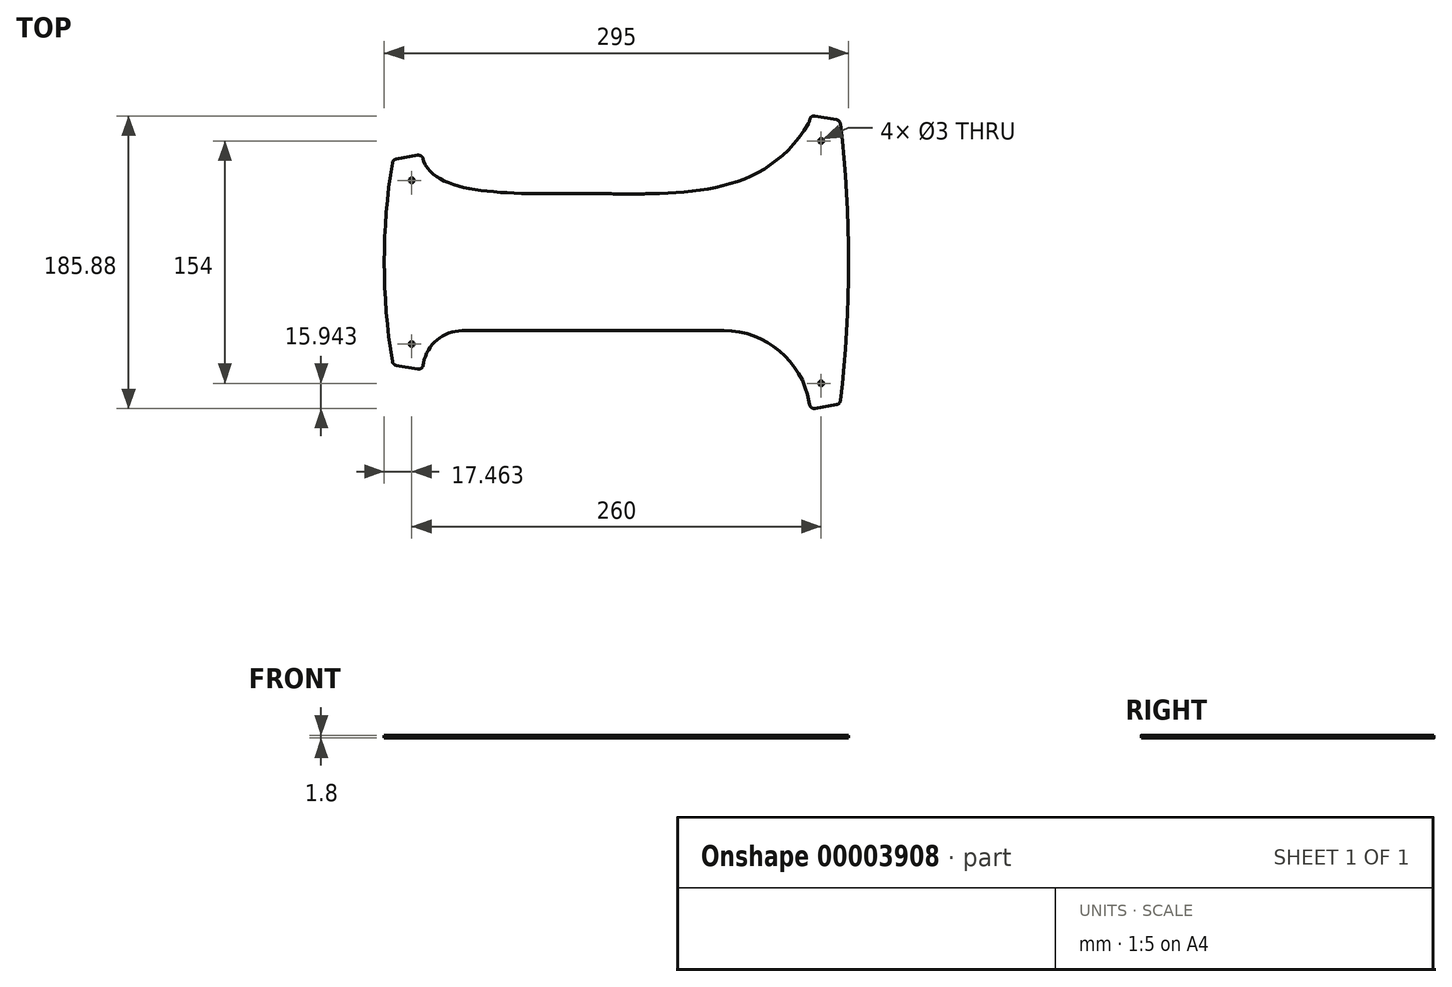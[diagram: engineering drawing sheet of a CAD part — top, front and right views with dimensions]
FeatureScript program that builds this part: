
annotation { "Feature Type Name" : "Feature", "Feature Type Description" : "" }
export const myFeature = defineFeature(function(context is Context, id is Id, definition is map)
    precondition{}
    {
        {
            var Q0;
            Q0=qCreatedBy(makeId("Top.planeOp"),FACE);
            var sketch = newSketch(context, id + "F0", { "sketchPlane" : qUnion([Q0])});
            skCircle(sketch, "E0", {"center": v(-144.57, -75.39) * mm, "radius": 1.5 * mm});
            skCircle(sketch, "E1", {"center": v(115.43, -100.39) * mm, "radius": 1.5 * mm});
            skLineSegment(sketch, "E2", {"start": v(132.97, -23.39) * mm, "end": v(-162.03, -23.39) * mm});
            skLineSegment(sketch, "E3", {"start": v(-154.44, -88.88) * mm, "end": v(-140.77, -91.29) * mm});
            skLineSegment(sketch, "E4", {"start": v(-137.3, -88.85) * mm, "end": v(-135.21, -77.04) * mm});
            skLineSegment(sketch, "E5", {"start": v(-135.21, -77.04) * mm, "end": v(-153.92, -73.74) * mm});
            skLineSegment(sketch, "E6", {"start": v(-153.92, -73.74) * mm, "end": v(-156.53, -88.5) * mm});
            skLineSegment(sketch, "E7", {"start": v(-137.06, -87.55) * mm, "end": v(-135.21, -77.04) * mm});
            skLineSegment(sketch, "E8", {"start": v(-112.44, -66.89) * mm, "end": v(53.73, -66.89) * mm});
            skLineSegment(sketch, "E9", {"start": v(-144.57, -75.39) * mm, "end": v(-171.48, -228.03) * mm});
            skLineSegment(sketch, "E10", {"start": v(106.08, -102.04) * mm, "end": v(124.79, -98.74) * mm});
            skLineSegment(sketch, "E11", {"start": v(124.79, -98.74) * mm, "end": v(127.4, -113.5) * mm});
            skLineSegment(sketch, "E12", {"start": v(125.2, -113.9) * mm, "end": v(111.64, -116.29) * mm});
            skLineSegment(sketch, "E13", {"start": v(108.16, -113.85) * mm, "end": v(106.08, -102.04) * mm});
            skLineSegment(sketch, "E14", {"start": v(115.43, -100.39) * mm, "end": v(138, -228.41) * mm});
            skLineSegment(sketch, "E15", {"start": v(107.9, -112.34) * mm, "end": v(106.08, -102.04) * mm});
            skPoint(sketch, "E16", {"position": v(122.82, -99.08) * mm});
            skPoint(sketch, "E17", {"position": v(108.05, -101.69) * mm});
            skLineSegment(sketch, "E18", {"start": v(108.05, -101.69) * mm, "end": v(99.36, -52.45) * mm});
            skLineSegment(sketch, "E19", {"start": v(99.36, -52.45) * mm, "end": v(114.14, -49.84) * mm});
            skLineSegment(sketch, "E20", {"start": v(114.14, -49.84) * mm, "end": v(122.82, -99.08) * mm});
            skPoint(sketch, "E21", {"position": v(-137.18, -76.69) * mm});
            skPoint(sketch, "E22", {"position": v(-151.95, -74.08) * mm});
            skLineSegment(sketch, "E23", {"start": v(-151.95, -74.08) * mm, "end": v(-144.14, -29.77) * mm});
            skLineSegment(sketch, "E24", {"start": v(-144.14, -29.77) * mm, "end": v(-129.37, -32.37) * mm});
            skLineSegment(sketch, "E25", {"start": v(-129.37, -32.37) * mm, "end": v(-137.18, -76.69) * mm});
            skCircle(sketch, "E26", {"center": v(-168, -208.34) * mm, "radius": 50 * mm});
            skCircle(sketch, "E27", {"center": v(134.53, -208.72) * mm, "radius": 50 * mm});
            skCircle(sketch, "E28", {"center": v(-144.57, 28.61) * mm, "radius": 1.5 * mm});
            skLineSegment(sketch, "E29", {"start": v(-144.14, -17) * mm, "end": v(-129.37, -14.4) * mm});
            skLineSegment(sketch, "E30", {"start": v(-129.37, -14.4) * mm, "end": v(-137.18, 29.92) * mm});
            skLineSegment(sketch, "E31", {"start": v(-137.18, 29.92) * mm, "end": v(-151.95, 27.31) * mm});
            skLineSegment(sketch, "E32", {"start": v(-151.95, 27.31) * mm, "end": v(-144.14, -17) * mm});
            skLineSegment(sketch, "E33", {"start": v(-137.18, 29.92) * mm, "end": v(-135.21, 30.26) * mm});
            skLineSegment(sketch, "E34", {"start": v(-151.95, 27.31) * mm, "end": v(-153.92, 26.96) * mm});
            skLineSegment(sketch, "E35", {"start": v(-135.21, 30.26) * mm, "end": v(-137.3, 42.08) * mm});
            skLineSegment(sketch, "E36", {"start": v(-140.77, 44.51) * mm, "end": v(-154.44, 42.1) * mm});
            skLineSegment(sketch, "E37", {"start": v(-156.53, 41.74) * mm, "end": v(-153.92, 26.96) * mm});
            skLineSegment(sketch, "E38", {"start": v(-112.44, 20.11) * mm, "end": v(53.73, 20.11) * mm});
            skLineSegment(sketch, "E39", {"start": v(-137.06, 40.77) * mm, "end": v(-135.21, 30.26) * mm});
            skCircle(sketch, "E40", {"center": v(115.43, 53.61) * mm, "radius": 1.5 * mm});
            skLineSegment(sketch, "E41", {"start": v(122.82, 52.31) * mm, "end": v(108.05, 54.92) * mm});
            skLineSegment(sketch, "E42", {"start": v(108.05, 54.92) * mm, "end": v(99.36, 5.68) * mm});
            skLineSegment(sketch, "E43", {"start": v(99.36, 5.68) * mm, "end": v(114.14, 3.07) * mm});
            skLineSegment(sketch, "E44", {"start": v(114.14, 3.07) * mm, "end": v(122.82, 52.31) * mm});
            skLineSegment(sketch, "E45", {"start": v(122.82, 52.31) * mm, "end": v(124.79, 51.96) * mm});
            skLineSegment(sketch, "E46", {"start": v(108.05, 54.92) * mm, "end": v(106.08, 55.26) * mm});
            skLineSegment(sketch, "E47", {"start": v(108.17, 66.78) * mm, "end": v(108.22, 67.07) * mm});
            skLineSegment(sketch, "E48", {"start": v(111.7, 69.5) * mm, "end": v(125.2, 67.12) * mm});
            skLineSegment(sketch, "E49", {"start": v(127.4, 66.74) * mm, "end": v(124.79, 51.96) * mm});
            skLineSegment(sketch, "E50", {"start": v(107.9, 65.56) * mm, "end": v(106.08, 55.26) * mm});
            skArc(sketch, "E51", {"start": v(-156.88, 39.64) * mm, "mid": v(-162.03, -23.39) * mm, "end": v(-156.88, -86.4) * mm});
            skArc(sketch, "E52", {"start": v(127.66, -111.3) * mm, "mid": v(132.97, -23.39) * mm, "end": v(127.66, 64.53) * mm});
            skPoint(sketch, "E53.visualSharp", {"position": v(-156.53, 41.74) * mm});
            skArc(sketch, "E53.filletArc", {"start": v(-154.44, 42.1) * mm, "mid": v(-156.05, 41.26) * mm, "end": v(-156.88, 39.64) * mm});
            skPoint(sketch, "E54.visualSharp", {"position": v(-137.82, 45.04) * mm});
            skArc(sketch, "E54.filletArc", {"start": v(-137.3, 42.08) * mm, "mid": v(-138.53, 44.02) * mm, "end": v(-140.77, 44.51) * mm});
            skPoint(sketch, "E55.visualSharp", {"position": v(-133.42, 20.11) * mm});
            skArc(sketch, "E55.filletArc", {"start": v(-137.06, 40.77) * mm, "mid": v(-128.51, 25.96) * mm, "end": v(-112.44, 20.11) * mm});
            skPoint(sketch, "E56.visualSharp", {"position": v(99.88, 20.11) * mm});
            skArc(sketch, "E56.filletArc", {"start": v(53.73, 20.11) * mm, "mid": v(89.08, 32.98) * mm, "end": v(107.9, 65.56) * mm});
            skPoint(sketch, "E57.visualSharp", {"position": v(108.75, 70.02) * mm});
            skArc(sketch, "E57.filletArc", {"start": v(111.7, 69.5) * mm, "mid": v(109.46, 69) * mm, "end": v(108.22, 67.07) * mm});
            skPoint(sketch, "E58.visualSharp", {"position": v(127.4, 66.74) * mm});
            skArc(sketch, "E58.filletArc", {"start": v(127.66, 64.53) * mm, "mid": v(126.86, 66.23) * mm, "end": v(125.2, 67.12) * mm});
            skPoint(sketch, "E59.visualSharp", {"position": v(127.4, -113.5) * mm});
            skArc(sketch, "E59.filletArc", {"start": v(125.2, -113.9) * mm, "mid": v(126.86, -113) * mm, "end": v(127.66, -111.3) * mm});
            skPoint(sketch, "E60.visualSharp", {"position": v(108.68, -116.8) * mm});
            skArc(sketch, "E60.filletArc", {"start": v(108.16, -113.85) * mm, "mid": v(109.4, -115.8) * mm, "end": v(111.64, -116.29) * mm});
            skPoint(sketch, "E61.visualSharp", {"position": v(99.88, -66.89) * mm});
            skArc(sketch, "E61.filletArc", {"start": v(107.9, -112.34) * mm, "mid": v(89.08, -79.75) * mm, "end": v(53.73, -66.89) * mm});
            skPoint(sketch, "E62.visualSharp", {"position": v(-133.42, -66.89) * mm});
            skArc(sketch, "E62.filletArc", {"start": v(-112.44, -66.89) * mm, "mid": v(-128.51, -72.74) * mm, "end": v(-137.06, -87.55) * mm});
            skPoint(sketch, "E63.visualSharp", {"position": v(-137.82, -91.8) * mm});
            skArc(sketch, "E63.filletArc", {"start": v(-140.77, -91.29) * mm, "mid": v(-138.53, -90.8) * mm, "end": v(-137.3, -88.85) * mm});
            skPoint(sketch, "E64.visualSharp", {"position": v(-156.53, -88.5) * mm});
            skArc(sketch, "E64.filletArc", {"start": v(-156.88, -86.4) * mm, "mid": v(-156.05, -88.03) * mm, "end": v(-154.44, -88.88) * mm});
            skPoint(sketch, "E65", {"position": v(-29.36, 20.11) * mm});
            skFitSpline(sketch, "E66", {"points": [v(107.9, 65.56) * mm, v(-29.36, 20.11) * mm, v(-137.06, 40.77) * mm], "startDerivative": vector(-160.74, -276.84) * mm, "endDerivative": vector(-62.92, 148.77) * mm});
            skArc(sketch, "E67.filletArc", {"start": v(107.43, 64.77) * mm, "mid": v(107.9, 65.74) * mm, "end": v(108.17, 66.78) * mm});
            skSolve(sketch);
        }
        {
            var Q0;
            {var subQ1=sQuery(id+"F0.wireOp",EDGE,"E33");Q0=makeQuery(id+"F0.imprint","IMPRINT",FACE,{"disambiguationData":[TD([[makeQuery(id+"F0.imprint","IMPRINT",EDGE,{"derivedFrom":subQ1}),1.0]])]});}
            var Q1;
            {var subQ5=sQuery(id+"F0.wireOp",EDGE,"E45");Q1=makeQuery(id+"F0.imprint","IMPRINT",FACE,{"disambiguationData":[TD([[makeQuery(id+"F0.imprint","IMPRINT",EDGE,{"derivedFrom":subQ5}),1.0]])]});}
            var Q2;
            {var subQ5=sQuery(id+"F0.wireOp",EDGE,"E6");Q2=makeQuery(id+"F0.imprint","IMPRINT",FACE,{"disambiguationData":[TD([[makeQuery(id+"F0.imprint","IMPRINT",EDGE,{"derivedFrom":subQ5}),1.0]])]});}
            var Q3;
            {var subQ8=sQuery(id+"F0.wireOp",EDGE,"E4");Q3=makeQuery(id+"F0.imprint","IMPRINT",FACE,{"disambiguationData":[TD([[makeQuery(id+"F0.imprint","IMPRINT",EDGE,{"derivedFrom":subQ8}),1.0]])]});}
            var Q4;
            {var subQ5=sQuery(id+"F0.wireOp",EDGE,"E13");Q4=makeQuery(id+"F0.imprint","IMPRINT",FACE,{"disambiguationData":[TD([[makeQuery(id+"F0.imprint","IMPRINT",EDGE,{"derivedFrom":subQ5}),-1.0]])]});}
            var Q5;
            {var subQ3=sQuery(id+"F0.wireOp",EDGE,"E11");Q5=makeQuery(id+"F0.imprint","IMPRINT",FACE,{"disambiguationData":[TD([[makeQuery(id+"F0.imprint","IMPRINT",EDGE,{"derivedFrom":subQ3}),-1.0]])]});}
            var Q6;
            {var subQ2=sQuery(id+"F0.wireOp",EDGE,"E2");Q6=makeQuery(id+"F0.imprint","IMPRINT",FACE,{"disambiguationData":[TD([[makeQuery(id+"F0.imprint","IMPRINT",EDGE,{"derivedFrom":subQ2}),-1.0]])]});}
            var Q7;
            {var subQ8=sQuery(id+"F0.wireOp",EDGE,"E2");Q7=makeQuery(id+"F0.imprint","IMPRINT",FACE,{"disambiguationData":[TD([[makeQuery(id+"F0.imprint","IMPRINT",EDGE,{"derivedFrom":subQ8}),1.0]])]});}
            var Q8;
            Q8=makeQuery(id+"F0.imprint","IMPRINT",FACE,{"disambiguationData":[TD([[makeQuery(id+"F0.imprint","IMPRINT",EDGE,{"derivedFrom":sQuery(id+"F0.wireOp",EDGE,"E29")}),1.0]])]});
            var Q9;
            {var subQ1=sQuery(id+"F0.wireOp",EDGE,"E23");Q9=makeQuery(id+"F0.imprint","IMPRINT",FACE,{"disambiguationData":[TD([[makeQuery(id+"F0.imprint","IMPRINT",EDGE,{"derivedFrom":subQ1}),-1.0]])]});}
            var Q10;
            {var subQ1=sQuery(id+"F0.wireOp",EDGE,"E18");Q10=makeQuery(id+"F0.imprint","IMPRINT",FACE,{"disambiguationData":[TD([[makeQuery(id+"F0.imprint","IMPRINT",EDGE,{"derivedFrom":subQ1}),-1.0]])]});}
            var Q11;
            {var subQ0=sQuery(id+"F0.wireOp",EDGE,"E42");Q11=makeQuery(id+"F0.imprint","IMPRINT",FACE,{"disambiguationData":[TD([[makeQuery(id+"F0.imprint","IMPRINT",EDGE,{"derivedFrom":subQ0}),1.0]])]});}
            var Q12;
            {var subQ1=sQuery(id+"F0.wireOp",EDGE,"E56.filletArc");Q12=makeQuery(id+"F0.imprint","IMPRINT",FACE,{"disambiguationData":[TD([[makeQuery(id+"F0.imprint","IMPRINT",EDGE,{"derivedFrom":subQ1}),1.0]])]});}
            var Q13;
            {var subQ3=sQuery(id+"F0.wireOp",EDGE,"E55.filletArc");Q13=makeQuery(id+"F0.imprint","IMPRINT",FACE,{"disambiguationData":[TD([[makeQuery(id+"F0.imprint","IMPRINT",EDGE,{"derivedFrom":subQ3}),1.0]])]});}
            extrude(context, id + "F1", {"entities" : qUnion([Q0, Q1, Q2, Q3, Q4, Q5, Q6, Q7, Q8, Q9, Q10, Q11, Q12, Q13]), "depth" : 1.8 * mm});
        }
    });
